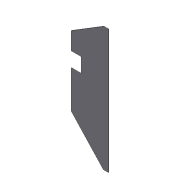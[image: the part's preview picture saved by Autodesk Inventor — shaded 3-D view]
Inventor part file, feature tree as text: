
AUTODESK INVENTOR PART (.ipt)
format: ipt  version: 2012 (Build 160160000, 160)  size: 94,720 bytes
history: native  units: in
note: dims shown in document units (in); Inventor stores cm internally (conversion verified against a paired STEP export)
features: extrude x3, sketch x3
ambient origin geometry x8: Origin, YZ Plane, XZ Plane, XY Plane, X Axis, Y Axis, Z Axis, Center Point
bodies: Solid1 (feature_tree)
feature tree (6):
  extrude  "Extrusion1"  Depth=25.0in
  extrude  "Extrusion2"  Depth=7.0in
  extrude  "ConveyorHole"  Depth=4.0in
  sketch  "Sketch1"  dims[d0=7.5in d1=25.0in]
  sketch  "Sketch2"  dims[d2=0.125in d3=0.0in d5=7.0in]
  sketch  "Sketch4"  dims[d6=0.125in d7=0.0in d8=4.0in d9=1.0in d17=3.0in d18=2.0in d19=1.0in d20=0.0in d27=7.5in]
